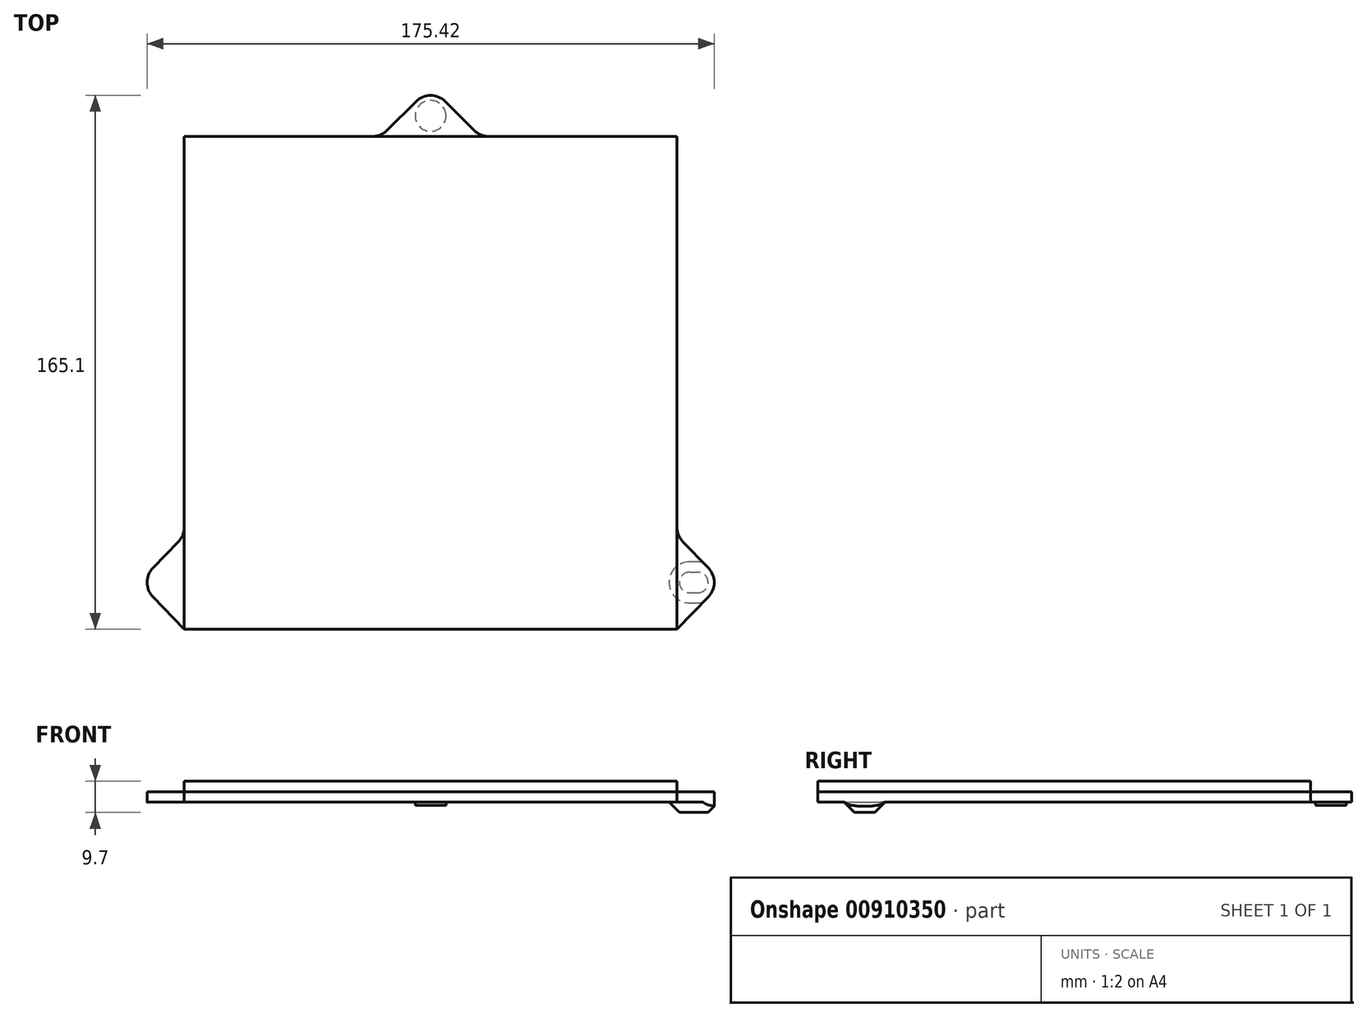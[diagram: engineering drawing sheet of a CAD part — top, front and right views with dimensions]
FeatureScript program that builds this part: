
annotation { "Feature Type Name" : "Feature", "Feature Type Description" : "" }
export const myFeature = defineFeature(function(context is Context, id is Id, definition is map)
    precondition{}
    {
        {
            var Q0;
            Q0=qCreatedBy(makeId("Top.planeOp"),FACE);
            var sketch = newSketch(context, id + "F0", { "sketchPlane" : qUnion([Q0])});
            skLineSegment(sketch, "E0.bottom", {"start": v(76.2, 76.2) * mm, "end": v(-76.2, 76.2) * mm});
            skLineSegment(sketch, "E0.top", {"start": v(76.2, -76.2) * mm, "end": v(-76.2, -76.2) * mm});
            skLineSegment(sketch, "E0.left", {"start": v(76.2, 76.2) * mm, "end": v(76.2, -76.2) * mm});
            skLineSegment(sketch, "E0.right", {"start": v(-76.2, 76.2) * mm, "end": v(-76.2, -76.2) * mm});
            skPoint(sketch, "E0.middle", {"position": v(0, 0) * mm});
            skSolve(sketch);
        }
        {
            var Q0;
            Q0 = qSketchRegion(id + "F0", true);
            extrude(context, id + "F1", {"entities" : qUnion([Q0]), "flatOperationType" : FlatOperationType.REMOVE, "depth" : 3.35 * mm, "offsetDistance" : 25.4 * mm, "domain" : OperationDomain.MODEL});
        }
        {
            var Q0;
            Q0=makeQuery(id+"F1.opExtrude","CAP_FACE",FACE,{"disambiguationData":[OSD([sQuery(id+"F0.wireOp",EDGE,"E0.bottom"),sQuery(id+"F0.wireOp",EDGE,"E0.top"),sQuery(id+"F0.wireOp",EDGE,"E0.left"),sQuery(id+"F0.wireOp",EDGE,"E0.right")])],"isStart":true});
            var sketch = newSketch(context, id + "F2", { "sketchPlane" : qUnion([Q0])});
            skLineSegment(sketch, "E1.0.0", {"start": v(76.2, 76.2) * mm, "end": v(-76.2, 76.2) * mm});
            skLineSegment(sketch, "E1.0.1", {"start": v(-76.2, 76.2) * mm, "end": v(-76.2, -76.2) * mm, "construction": true});
            skLineSegment(sketch, "E1.0.3", {"start": v(76.2, -76.2) * mm, "end": v(76.2, 76.2) * mm, "construction": true});
            skLineSegment(sketch, "E2", {"start": v(76.2, -76.2) * mm, "end": v(76.2, 47.3) * mm});
            skLineSegment(sketch, "E3", {"start": v(76.2, 47.3) * mm, "end": v(85.92, 57.33) * mm});
            skLineSegment(sketch, "E4", {"start": v(76.2, 76.2) * mm, "end": v(85.92, 66.16) * mm});
            skArc(sketch, "E5", {"start": v(85.92, 57.33) * mm, "mid": v(87.7, 61.75) * mm, "end": v(85.92, 66.16) * mm});
            skLineSegment(sketch, "E6", {"start": v(-76.2, 76.2) * mm, "end": v(-85.92, 66.16) * mm});
            skLineSegment(sketch, "E7", {"start": v(-76.2, -76.2) * mm, "end": v(-76.2, 47.3) * mm});
            skLineSegment(sketch, "E8", {"start": v(-76.2, 47.3) * mm, "end": v(-85.92, 57.33) * mm});
            skArc(sketch, "E9", {"start": v(-85.92, 66.16) * mm, "mid": v(-87.7, 61.75) * mm, "end": v(-85.92, 57.33) * mm});
            skLineSegment(sketch, "E10", {"start": v(-81.36, 61.75) * mm, "end": v(81.36, 61.75) * mm, "construction": true});
            skLineSegment(sketch, "E11", {"start": v(0, 76.2) * mm, "end": v(0, 61.75) * mm, "construction": true});
            skLineSegment(sketch, "E12", {"start": v(-15.33, -76.2) * mm, "end": v(-4.5, -87.04) * mm});
            skLineSegment(sketch, "E13", {"start": v(4.5, -87.04) * mm, "end": v(15.33, -76.2) * mm});
            skLineSegment(sketch, "E14", {"start": v(-76.2, -76.2) * mm, "end": v(-15.33, -76.2) * mm});
            skLineSegment(sketch, "E15", {"start": v(15.33, -76.2) * mm, "end": v(76.2, -76.2) * mm});
            skArc(sketch, "E16", {"start": v(-4.5, -87.04) * mm, "mid": v(0, -88.9) * mm, "end": v(4.5, -87.04) * mm});
            skSolve(sketch);
        }
        {
            var Q0;
            Q0 = qSketchRegion(id + "F2", true);
            extrude(context, id + "F3", {"entities" : qUnion([Q0]), "depth" : 6.35 * mm, "offsetDistance" : 25.4 * mm});
        }
        {
            var Q0;
            Q0=makeQuery(id+"F3.opExtrude","SWEPT_EDGE",EDGE,{"disambiguationData":[OSD([sQuery(id+"F0.wireOp",EDGE,"E0.right"),sQuery(id+"F2.wireOp",EDGE,"E7"),sQuery(id+"F2.wireOp",EDGE,"E8")])]});
            var Q1;
            Q1=makeQuery(id+"F3.opExtrude","SWEPT_EDGE",EDGE,{"disambiguationData":[OSD([sQuery(id+"F0.wireOp",EDGE,"E0.left"),sQuery(id+"F2.wireOp",EDGE,"E2"),sQuery(id+"F2.wireOp",EDGE,"E3")])]});
            var Q2;
            Q2=makeQuery(id+"F3.opExtrude","SWEPT_EDGE",EDGE,{"disambiguationData":[OSD([sQuery(id+"F0.wireOp",EDGE,"E0.bottom"),sQuery(id+"F2.wireOp",EDGE,"E13"),sQuery(id+"F2.wireOp",EDGE,"E15")])]});
            var Q3;
            Q3=makeQuery(id+"F3.opExtrude","SWEPT_EDGE",EDGE,{"disambiguationData":[OSD([sQuery(id+"F0.wireOp",EDGE,"E0.bottom"),sQuery(id+"F2.wireOp",EDGE,"E12"),sQuery(id+"F2.wireOp",EDGE,"E14")])]});
            fillet(context, id + "F4", {"entities" : qUnion([Q0, Q1, Q2, Q3]), "radius" : 6.35 * mm, "tangentPropagation" : true, "allowEdgeOverflow" : false});
        }
        {
            var Q0;
            Q0=makeQuery(id+"F3.opExtrude","CAP_FACE",FACE,{"disambiguationData":[OSD([sQuery(id+"F2.wireOp",EDGE,"E1.0.0"),sQuery(id+"F2.wireOp",EDGE,"E1.0.2"),sQuery(id+"F2.wireOp",EDGE,"E2"),sQuery(id+"F2.wireOp",EDGE,"E3"),sQuery(id+"F2.wireOp",EDGE,"E4"),sQuery(id+"F2.wireOp",EDGE,"E5"),sQuery(id+"F2.wireOp",EDGE,"E6"),sQuery(id+"F2.wireOp",EDGE,"E7"),sQuery(id+"F2.wireOp",EDGE,"E8"),sQuery(id+"F2.wireOp",EDGE,"E9")])],"isStart":false});
            var sketch = newSketch(context, id + "F5", { "sketchPlane" : qUnion([Q0])});
            skCircle(sketch, "E17", {"center": v(-81.36, 61.75) * mm, "radius": 3.18 * mm});
            skLineSegment(sketch, "E18", {"start": v(80.09, 61.75) * mm, "end": v(82.63, 61.75) * mm});
            skPoint(sketch, "E19", {"position": v(81.36, 61.75) * mm});
            skArc(sketch, "E20.0.startCap", {"start": v(80.09, 58.57) * mm, "mid": v(76.91, 61.75) * mm, "end": v(80.09, 64.92) * mm});
            skArc(sketch, "E20.0.endCap", {"start": v(82.63, 64.92) * mm, "mid": v(85.8, 61.75) * mm, "end": v(82.63, 58.57) * mm});
            skLineSegment(sketch, "E20.0.left", {"start": v(80.09, 64.92) * mm, "end": v(82.63, 64.92) * mm});
            skLineSegment(sketch, "E20.0.right", {"start": v(80.09, 58.57) * mm, "end": v(82.63, 58.57) * mm});
            skCircle(sketch, "E21", {"center": v(0, -82.55) * mm, "radius": 4.76 * mm});
            skCircle(sketch, "E22", {"center": v(-36.63, -84.28) * mm, "radius": 2.38 * mm});
            skLineSegment(sketch, "E23", {"start": v(-42.77, -83.45) * mm, "end": v(-39.17, -83.45) * mm});
            skLineSegment(sketch, "E24", {"start": v(-39.17, -83.45) * mm, "end": v(-36.63, -80.91) * mm});
            skLineSegment(sketch, "E25", {"start": v(-36.63, -80.91) * mm, "end": v(-34.1, -83.45) * mm});
            skLineSegment(sketch, "E26", {"start": v(-34.1, -83.45) * mm, "end": v(-30.5, -83.45) * mm});
            skSolve(sketch);
        }
        {
            var Q0;
            Q0=makeQuery(id+"F5.imprint","IMPRINT",FACE,{"disambiguationData":[TD([[makeQuery(id+"F5.imprint","IMPRINT",EDGE,{"derivedFrom":sQuery(id+"F5.wireOp",EDGE,"E17")}),1.0]])]});
            var Q1;
            Q1=makeQuery(id+"F5.imprint","IMPRINT",FACE,{"disambiguationData":[TD([[makeQuery(id+"F5.imprint","IMPRINT",EDGE,{"derivedFrom":sQuery(id+"F5.wireOp",EDGE,"E20.0.startCap")}),-1.0]])]});
            extrude(context, id + "F6", {"entities" : qUnion([Q0, Q1]), "operationType" : NewBodyOperationType.REMOVE, "oppositeDirection" : true, "depth" : 3.17 * mm, "offsetDistance" : 25.4 * mm});
        }
        {
            var Q0;
            Q0=makeQuery(id+"F6.boolean.opBoolean","COPY",EDGE,{"derivedFrom":makeQuery(id+"F6.opExtrude","CAP_EDGE",EDGE,{"disambiguationData":[OSD([sQuery(id+"F5.wireOp",EDGE,"E17")])],"isStart":false})});
            var Q1;
            Q1=makeQuery(id+"F6.boolean.opBoolean","COPY",EDGE,{"derivedFrom":makeQuery(id+"F6.opExtrude","CAP_EDGE",EDGE,{"disambiguationData":[OSD([sQuery(id+"F5.wireOp",EDGE,"E20.0.startCap")])],"isStart":false})});
            chamfer(context, id + "F7", {"entities" : qUnion([Q0, Q1]), "width" : 3.17 * mm, "tangentPropagation" : true});
        }
        {
            var Q0;
            Q0=makeQuery(id+"F5.imprint","IMPRINT",FACE,{"disambiguationData":[TD([[makeQuery(id+"F5.imprint","IMPRINT",EDGE,{"derivedFrom":sQuery(id+"F5.wireOp",EDGE,"E21")}),1.0]])]});
            extrude(context, id + "F8", {"entities" : qUnion([Q0]), "operationType" : NewBodyOperationType.REMOVE, "oppositeDirection" : true, "depth" : 2.18 * mm, "offsetDistance" : 25.4 * mm});
        }
    });
